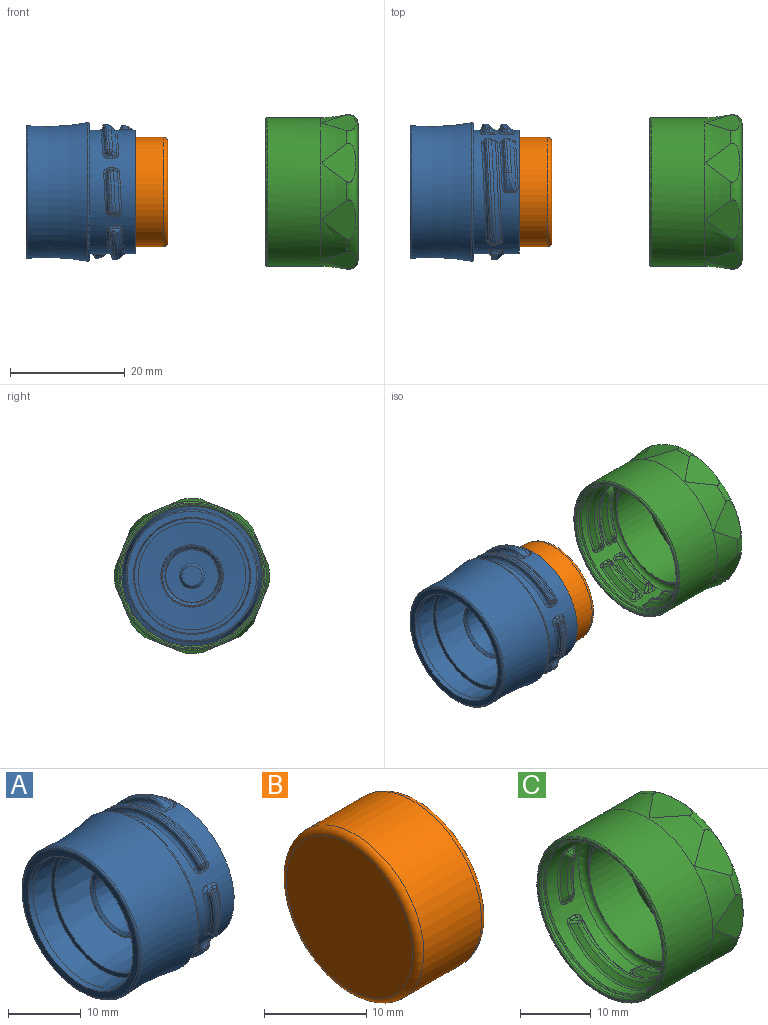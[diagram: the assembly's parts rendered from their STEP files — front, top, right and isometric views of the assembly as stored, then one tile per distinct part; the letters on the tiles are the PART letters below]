
ASSEMBLY  parts=3 mates=2
PART A: 206 faces, bbox 54.1x48.6x48.6 mm
  f0: bspline ~20.51x6.46mm, area 20.2mm2, adj f18,f76,f136,f188
  f1: bspline ~10.25x6.46mm, area 8.1mm2, adj f19,f60,f100,f196
  f2: bspline ~20.51x6.46mm, area 20.2mm2, adj f20,f106,f112,f156
  f3: bspline ~11.84x4.34mm, area 7mm2, adj f21,f82,f118,f180
  f4: bspline ~11.84x4.34mm, area 7mm2, adj f22,f88,f124,f172
  f5: bspline ~11.84x4.34mm, area 7mm2, adj f23,f94,f130,f164
  f6: bspline ~20.51x6.46mm, area 9.1mm2, adj f24,f81,f141,f195
  f7: bspline ~10.25x6.46mm, area 3.6mm2, adj f25,f63,f105,f203
  f8: bspline ~20.51x6.46mm, area 9.1mm2, adj f26,f111,f117,f163
  f9: bspline ~11.84x4.34mm, area 3.1mm2, adj f27,f87,f123,f187
  f10: bspline ~11.84x4.34mm, area 3.1mm2, adj f28,f93,f129,f179
  f11: bspline ~11.84x4.34mm, area 3.1mm2, adj f29,f99,f135,f171
  f12: cylinder r=11.84mm len=18.47mm, axis (-1,0,0), area 7.6mm2, adj f18,f24,f78,f80,f138,f139
  f13: cylinder r=11.84mm len=5.9mm, axis (-1,0,0), area 2.6mm2, adj f19,f25,f57,f102,f104
  f14: cylinder r=11.84mm len=18.47mm, axis (-1,0,0), area 7.6mm2, adj f20,f26,f108,f110,f114,f115
  f15: cylinder r=11.84mm len=7.03mm, axis (-1,0,0), area 2.6mm2, adj f21,f27,f84,f85,f120,f122
  f16: cylinder r=11.84mm len=7.03mm, axis (-1,0,0), area 2.6mm2, adj f22,f28,f90,f91,f126,f128
  f17: cylinder r=11.84mm len=7.03mm, axis (-1,0,0), area 2.6mm2, adj f23,f29,f96,f97,f132,f134
  f18: bspline ~19.36x5.44mm, area 12.6mm2, adj f0,f12,f77,f137
  f19: bspline ~7.42x4.83mm, area 4.3mm2, adj f1,f13,f60,f101
  f20: bspline ~19.93x5.61mm, area 12.6mm2, adj f2,f14,f107,f113
  f21: bspline ~8.49x1.01mm, area 4.3mm2, adj f3,f15,f83,f119
  f22: bspline ~8.49x1.09mm, area 4.3mm2, adj f4,f16,f89,f125
  f23: bspline ~8.48x1.05mm, area 4.3mm2, adj f5,f17,f95,f131
  f24: bspline ~19.36x5.35mm, area 7.4mm2, adj f6,f12,f80,f139
  f25: bspline ~7.72x4.94mm, area 2.5mm2, adj f7,f13,f63,f104
  f26: bspline ~19.35x5.52mm, area 7.4mm2, adj f8,f14,f110,f115
  f27: bspline ~8.48x1.03mm, area 2.5mm2, adj f9,f15,f85,f122
  f28: bspline ~8.48x1.11mm, area 2.5mm2, adj f10,f16,f91,f128
  f29: bspline ~8.48x1.01mm, area 2.5mm2, adj f11,f17,f97,f134
  f30: torus R=49.49mm, axis (1,0,0), area 766.5mm2, adj f204,f205
  f31: cone r=4.57mm half-angle=1deg, axis (-1,0,0), area 137.6mm2, adj f40,f46
  f32: cone r=9.55mm half-angle=88.5deg, axis (-1,0,0), area 193.8mm2, adj f36,f37
  f33: plane 22.56x22.56mm, normal (-1,0,0), area 74.4mm2, adj f47,f205
  f34: plane 20.17x20.17mm, normal (-1,0,0), area 43.5mm2, adj f35,f36
  f35: cone r=10.01mm half-angle=1deg, axis (1,0,0), area 224.6mm2, adj f34,f47
  f36: cone r=9.3mm half-angle=1deg, axis (1,0,0), area 617.8mm2, adj f32,f34
  f37: cone r=5.46mm half-angle=1deg, axis (1,0,0), area 261mm2, adj f32,f38
  f38: plane 10.61x10.61mm, normal (-1,0,0), area 5.7mm2, adj f37,f46
  f39: cone r=4.85mm half-angle=58.5deg, axis (-1,0,0), area 7.9mm2, adj f41,f45
  f40: cone r=4.22mm half-angle=58.5deg, axis (1,0,0), area 7.5mm2, adj f31,f41
  f41: cylinder r=4.85mm len=9.7mm, axis (1,0,0), area 11.6mm2, adj f39,f40
  f42: plane 3.51x3.51mm, normal (-1,0,0), area 9.6mm2, adj f43
  f43: cone r=1.75mm half-angle=45deg, axis (1,0,0), area 7.8mm2, adj f42,f44
  f44: cone r=9.55mm half-angle=88.5deg, axis (-1,0,0), area 51mm2, adj f43,f45
  f45: cone r=4.57mm half-angle=1deg, axis (-1,0,0), area 58.2mm2, adj f39,f44
  f46: cone r=5.13mm half-angle=45.5deg, axis (-1,0,0), area 17.9mm2, adj f31,f38
  f47: cone r=10.02mm half-angle=11deg, axis (-1,0,0), area 50.9mm2, adj f33,f35
  f48: plane 23.63x23.63mm, normal (1,0,0), area 74.3mm2, adj f49,f204
  f49: cylinder r=10.77mm len=21.54mm, axis (1,0,0), area 290.6mm2, adj f48,f52,f148,f149,f150,f151,f152,f153
  f50: plane 20.09x20.09mm, normal (1,0,0), area 317mm2, adj f51
  f51: cylinder r=10.04mm len=20.09mm, axis (1,0,0), area 195.6mm2, adj f50,f52
  f52: plane 21.54x21.54mm, normal (1,0,0), area 47.4mm2, adj f49,f51
  f53: bspline ~10.25x6.46mm, area 8.1mm2, adj f58,f59,f142,f148
  f54: bspline ~10.25x6.46mm, area 3.6mm2, adj f61,f62,f147,f155
  f55: cylinder r=11.84mm len=5.9mm, axis (-1,0,0), area 2.6mm2, adj f56,f59,f62,f144,f145
  f56: cylinder r=3.81mm len=3.21mm, axis (-1,0,0), area 2.4mm2, adj f55,f58,f61,f152
  f57: cylinder r=3.81mm len=3.21mm, axis (-1,0,0), area 2.4mm2, adj f13,f60,f63,f199
  f58: bspline ~4x1.34mm, area 2mm2, adj f53,f56,f59,f150
  f59: bspline ~6.61x4.58mm, area 4.3mm2, adj f53,f55,f58,f143
  f60: bspline ~4.04x1.6mm, area 2mm2, adj f1,f19,f57,f197
  f61: bspline ~3.63x0.96mm, area 1.1mm2, adj f54,f56,f62,f154
  f62: bspline ~7.86x4.78mm, area 2.5mm2, adj f54,f55,f61,f145
  f63: bspline ~4.19x0.96mm, area 1mm2, adj f7,f25,f57,f201
  f64: plane 0.75x0.38mm, normal (0,0.84,0.54), area 0.2mm2, adj f142,f143,f144,f147,f151
  f65: plane 0.75x0.45mm, normal (0,0.02,-1), area 0.2mm2, adj f130,f131,f132,f135,f168
  f66: plane 0.75x0.45mm, normal (0,0.02,-1), area 0.2mm2, adj f124,f125,f126,f129,f176
  f67: plane 0.75x0.38mm, normal (0,0.84,0.54), area 0.2mm2, adj f136,f137,f138,f141,f191
  f68: plane 0.75x0.38mm, normal (0,-0.84,-0.54), area 0.2mm2, adj f112,f113,f114,f117,f159
  f69: plane 0.75x0.45mm, normal (0,-0.02,1), area 0.2mm2, adj f118,f119,f120,f123,f184
  f70: plane 0.75x0.45mm, normal (0,0.02,1), area 0.2mm2, adj f94,f95,f96,f99,f167
  f71: plane 0.75x0.38mm, normal (0,0.84,-0.54), area 0.2mm2, adj f106,f107,f108,f111,f160
  f72: plane 0.75x0.45mm, normal (0,0.02,1), area 0.2mm2, adj f88,f89,f90,f93,f175
  f73: plane 0.75x0.38mm, normal (0,0.84,-0.54), area 0.2mm2, adj f100,f101,f102,f105,f200
  f74: plane 0.75x0.38mm, normal (0,-0.84,0.54), area 0.2mm2, adj f76,f77,f78,f81,f192
  f75: plane 0.75x0.45mm, normal (0,-0.02,-1), area 0.2mm2, adj f82,f83,f84,f87,f183
  f76: bspline ~1.4x1.37mm, area 0.5mm2, adj f0,f74,f77,f190
  f77: bspline ~0.71x0.7mm, area 0.3mm2, adj f18,f74,f76,f78
  f78: cylinder r=0.51mm len=0.59mm, axis (-1,0,0), area 0.2mm2, adj f12,f74,f77,f79
  f79: bspline ~0.66x0.46mm, area 0.1mm2, adj f78,f80,f81
  f80: bspline ~0.35x0.34mm, area 0mm2, adj f12,f24,f79,f81
  f81: bspline ~1.22x0.98mm, area 0.4mm2, adj f6,f74,f79,f80,f194
  f82: bspline ~1.35x1.33mm, area 0.5mm2, adj f3,f75,f83,f181
  f83: bspline ~0.74x0.57mm, area 0.3mm2, adj f21,f75,f82,f84
  f84: cylinder r=0.51mm len=0.48mm, axis (-1,0,0), area 0.2mm2, adj f15,f75,f83,f86
  f85: bspline ~0.32x0.27mm, area 0mm2, adj f15,f27,f86,f87
  f86: bspline ~0.5x0.46mm, area 0.1mm2, adj f84,f85,f87
  f87: bspline ~1.01x0.64mm, area 0.4mm2, adj f9,f75,f85,f86,f185
  f88: bspline ~1.35x1.33mm, area 0.5mm2, adj f4,f72,f89,f173
  f89: bspline ~0.74x0.57mm, area 0.3mm2, adj f22,f72,f88,f90
  f90: cylinder r=0.51mm len=0.48mm, axis (-1,0,0), area 0.2mm2, adj f16,f72,f89,f92
  f91: bspline ~0.32x0.27mm, area 0mm2, adj f16,f28,f92,f93
  f92: bspline ~0.5x0.46mm, area 0.1mm2, adj f90,f91,f93
  f93: bspline ~1.01x0.64mm, area 0.4mm2, adj f10,f72,f91,f92,f177
  f94: bspline ~1.35x1.33mm, area 0.5mm2, adj f5,f70,f95,f165
  f95: bspline ~0.74x0.57mm, area 0.3mm2, adj f23,f70,f94,f96
  f96: cylinder r=0.51mm len=0.48mm, axis (-1,0,0), area 0.2mm2, adj f17,f70,f95,f98
  f97: bspline ~0.32x0.27mm, area 0mm2, adj f17,f29,f98,f99
  f98: bspline ~0.5x0.46mm, area 0.1mm2, adj f96,f97,f99
  f99: bspline ~1.01x0.64mm, area 0.4mm2, adj f11,f70,f97,f98,f169
  f100: bspline ~1.4x1.37mm, area 0.5mm2, adj f1,f73,f101,f198
  f101: bspline ~0.71x0.7mm, area 0.3mm2, adj f19,f73,f100,f102
  f102: cylinder r=0.51mm len=0.59mm, axis (-1,0,0), area 0.2mm2, adj f13,f73,f101,f103
  f103: bspline ~0.66x0.46mm, area 0.1mm2, adj f102,f104,f105
  f104: bspline ~0.35x0.34mm, area 0mm2, adj f13,f25,f103,f105
  f105: bspline ~1.22x0.98mm, area 0.4mm2, adj f7,f73,f103,f104,f202
  f106: bspline ~1.4x1.37mm, area 0.5mm2, adj f2,f71,f107,f158
  f107: bspline ~0.71x0.7mm, area 0.3mm2, adj f20,f71,f106,f108
  f108: cylinder r=0.51mm len=0.59mm, axis (-1,0,0), area 0.2mm2, adj f14,f71,f107,f109
  f109: bspline ~0.66x0.46mm, area 0.1mm2, adj f108,f110,f111
  f110: bspline ~0.35x0.34mm, area 0mm2, adj f14,f26,f109,f111
  f111: bspline ~1.22x0.98mm, area 0.4mm2, adj f8,f71,f109,f110,f162
  f112: bspline ~1.41x1.38mm, area 0.5mm2, adj f2,f68,f113,f157
  f113: bspline ~0.74x0.67mm, area 0.3mm2, adj f20,f68,f112,f114
  f114: cylinder r=0.51mm len=0.59mm, axis (-1,0,0), area 0.2mm2, adj f14,f68,f113,f116
  f115: bspline ~0.35x0.34mm, area 0mm2, adj f14,f26,f116,f117
  f116: bspline ~0.66x0.46mm, area 0.1mm2, adj f114,f115,f117
  f117: bspline ~1.06x0.86mm, area 0.4mm2, adj f8,f68,f115,f116,f161
  f118: bspline ~1.36x1.32mm, area 0.5mm2, adj f3,f69,f119,f182
  f119: bspline ~0.7x0.61mm, area 0.3mm2, adj f21,f69,f118,f120
  f120: cylinder r=0.51mm len=0.48mm, axis (-1,0,0), area 0.2mm2, adj f15,f69,f119,f121
  f121: bspline ~0.5x0.46mm, area 0.1mm2, adj f120,f122,f123
  f122: bspline ~0.33x0.26mm, area 0mm2, adj f15,f27,f121,f123
  f123: bspline ~1.17x0.7mm, area 0.4mm2, adj f9,f69,f121,f122,f186
  f124: bspline ~1.36x1.32mm, area 0.5mm2, adj f4,f66,f125,f174
  f125: bspline ~0.7x0.61mm, area 0.3mm2, adj f22,f66,f124,f126
  f126: cylinder r=0.51mm len=0.48mm, axis (-1,0,0), area 0.2mm2, adj f16,f66,f125,f127
  f127: bspline ~0.5x0.46mm, area 0.1mm2, adj f126,f128,f129
  f128: bspline ~0.33x0.26mm, area 0mm2, adj f16,f28,f127,f129
  f129: bspline ~1.17x0.7mm, area 0.4mm2, adj f10,f66,f127,f128,f178
  f130: bspline ~1.36x1.32mm, area 0.5mm2, adj f5,f65,f131,f166
  f131: bspline ~0.7x0.61mm, area 0.3mm2, adj f23,f65,f130,f132
  f132: cylinder r=0.51mm len=0.48mm, axis (-1,0,0), area 0.2mm2, adj f17,f65,f131,f133
  f133: bspline ~0.5x0.46mm, area 0.1mm2, adj f132,f134,f135
  f134: bspline ~0.33x0.26mm, area 0mm2, adj f17,f29,f133,f135
  f135: bspline ~1.17x0.7mm, area 0.4mm2, adj f11,f65,f133,f134,f170
  f136: bspline ~1.41x1.38mm, area 0.5mm2, adj f0,f67,f137,f189
  f137: bspline ~0.74x0.67mm, area 0.3mm2, adj f18,f67,f136,f138
  f138: cylinder r=0.51mm len=0.59mm, axis (-1,0,0), area 0.2mm2, adj f12,f67,f137,f140
  f139: bspline ~0.35x0.34mm, area 0mm2, adj f12,f24,f140,f141
  f140: bspline ~0.66x0.46mm, area 0.1mm2, adj f138,f139,f141
  f141: bspline ~1.06x0.86mm, area 0.4mm2, adj f6,f67,f139,f140,f193
  f142: bspline ~1.41x1.38mm, area 0.5mm2, adj f53,f64,f143,f149
  f143: bspline ~0.74x0.67mm, area 0.3mm2, adj f59,f64,f142,f144
  f144: cylinder r=0.51mm len=0.59mm, axis (-1,0,0), area 0.2mm2, adj f55,f64,f143,f146
  f145: bspline ~0.35x0.34mm, area 0mm2, adj f55,f62,f146,f147
  f146: bspline ~0.66x0.46mm, area 0.1mm2, adj f144,f145,f147
  f147: bspline ~1.06x0.86mm, area 0.4mm2, adj f54,f64,f145,f146,f153
  f148: bspline ~10.19x6.22mm, area 3.7mm2, adj f49,f53,f149,f150
  f149: bspline ~1.52x0.78mm, area 0.5mm2, adj f49,f142,f148,f151
  f150: bspline ~1.23x0.84mm, area 0.3mm2, adj f49,f58,f148,f152
  f151: cylinder r=0.51mm len=0.75mm, axis (1,0,0), area 0.4mm2, adj f49,f64,f149,f153
  f152: cylinder r=0.51mm len=1.38mm, axis (1,0,0), area 0.4mm2, adj f49,f56,f150,f154
  f153: bspline ~1.17x1.03mm, area 0.7mm2, adj f49,f147,f151,f155
  f154: bspline ~1.45x0.75mm, area 0.7mm2, adj f49,f61,f152,f155
  f155: bspline ~10.24x5.89mm, area 6.2mm2, adj f49,f54,f153,f154
  f156: bspline ~19.7x6.27mm, area 8mm2, adj f2,f49,f157,f158
  f157: bspline ~1.52x0.78mm, area 0.5mm2, adj f49,f112,f156,f159
  f158: bspline ~1.5x0.83mm, area 0.5mm2, adj f49,f106,f156,f160
  f159: cylinder r=0.51mm len=0.75mm, axis (1,0,0), area 0.4mm2, adj f49,f68,f157,f161
  f160: cylinder r=0.51mm len=0.75mm, axis (1,0,0), area 0.4mm2, adj f49,f71,f158,f162
  f161: bspline ~1.17x1.03mm, area 0.7mm2, adj f49,f117,f159,f163
  f162: bspline ~1.21x1.2mm, area 0.7mm2, adj f49,f111,f160,f163
  f163: bspline ~19.45x5.88mm, area 14mm2, adj f8,f49,f161,f162
  f164: bspline ~10.04x1.63mm, area 2.8mm2, adj f5,f49,f165,f166
  f165: bspline ~1.52x0.83mm, area 0.5mm2, adj f49,f94,f164,f167
  f166: bspline ~1.5x0.91mm, area 0.5mm2, adj f49,f130,f164,f168
  f167: cylinder r=0.51mm len=0.75mm, axis (1,0,0), area 0.4mm2, adj f49,f70,f165,f169
  f168: cylinder r=0.51mm len=0.75mm, axis (1,0,0), area 0.4mm2, adj f49,f65,f166,f170
  f169: bspline ~1.11x1.03mm, area 0.7mm2, adj f49,f99,f167,f171
  f170: bspline ~1.2x1.19mm, area 0.7mm2, adj f49,f135,f168,f171
  f171: bspline ~8.76x1.55mm, area 4.8mm2, adj f11,f49,f169,f170
  f172: bspline ~10.04x1.63mm, area 2.8mm2, adj f4,f49,f173,f174
  f173: bspline ~1.52x0.83mm, area 0.5mm2, adj f49,f88,f172,f175
  f174: bspline ~1.5x0.91mm, area 0.5mm2, adj f49,f124,f172,f176
  f175: cylinder r=0.51mm len=0.75mm, axis (1,0,0), area 0.4mm2, adj f49,f72,f173,f177
  f176: cylinder r=0.51mm len=0.75mm, axis (1,0,0), area 0.4mm2, adj f49,f66,f174,f178
  f177: bspline ~1.11x1.03mm, area 0.7mm2, adj f49,f93,f175,f179
  f178: bspline ~1.2x1.19mm, area 0.7mm2, adj f49,f129,f176,f179
  f179: bspline ~9.91x1.55mm, area 4.8mm2, adj f10,f49,f177,f178
  f180: bspline ~10.04x1.63mm, area 2.8mm2, adj f3,f49,f181,f182
  f181: bspline ~1.52x0.83mm, area 0.5mm2, adj f49,f82,f180,f183
  f182: bspline ~1.5x0.91mm, area 0.5mm2, adj f49,f118,f180,f184
  f183: cylinder r=0.51mm len=0.75mm, axis (1,0,0), area 0.4mm2, adj f49,f75,f181,f185
  f184: cylinder r=0.51mm len=0.75mm, axis (1,0,0), area 0.4mm2, adj f49,f69,f182,f186
  f185: bspline ~1.11x1.03mm, area 0.7mm2, adj f49,f87,f183,f187
  f186: bspline ~1.2x1.19mm, area 0.7mm2, adj f49,f123,f184,f187
  f187: bspline ~8.76x1.55mm, area 4.8mm2, adj f9,f49,f185,f186
  f188: bspline ~19.7x6.27mm, area 8mm2, adj f0,f49,f189,f190
  f189: bspline ~1.52x0.78mm, area 0.5mm2, adj f49,f136,f188,f191
  f190: bspline ~1.5x0.83mm, area 0.5mm2, adj f49,f76,f188,f192
  f191: cylinder r=0.51mm len=0.75mm, axis (1,0,0), area 0.4mm2, adj f49,f67,f189,f193
  f192: cylinder r=0.51mm len=0.75mm, axis (1,0,0), area 0.4mm2, adj f49,f74,f190,f194
  f193: bspline ~1.17x1.03mm, area 0.7mm2, adj f49,f141,f191,f195
  f194: bspline ~1.21x1.2mm, area 0.7mm2, adj f49,f81,f192,f195
  f195: bspline ~19.45x5.88mm, area 14mm2, adj f6,f49,f193,f194
  f196: bspline ~10.13x6.26mm, area 3.7mm2, adj f1,f49,f197,f198
  f197: bspline ~1.32x1.04mm, area 0.4mm2, adj f49,f60,f196,f199
  f198: bspline ~1.17x0.83mm, area 0.5mm2, adj f49,f100,f196,f200
  f199: cylinder r=0.51mm len=1.35mm, axis (1,0,0), area 0.4mm2, adj f49,f57,f197,f201
  f200: cylinder r=0.51mm len=0.75mm, axis (1,0,0), area 0.4mm2, adj f49,f73,f198,f202
  f201: bspline ~1.79x0.73mm, area 0.6mm2, adj f49,f63,f199,f203
  f202: bspline ~1.21x1.2mm, area 0.7mm2, adj f49,f105,f200,f203
  f203: bspline ~10.24x5.83mm, area 6.2mm2, adj f7,f49,f201,f202
  f204: torus R=11.82mm, axis (-1,0,0), area 33.7mm2, adj f30,f48
  f205: torus R=11.28mm, axis (-1,0,0), area 30.3mm2, adj f30,f33
PART B: 5 faces, bbox 9.5x20.6x20.6 mm
  f0: cylinder r=9.53mm len=19.05mm, axis (-1,0,0), area 478.8mm2, adj f3,f4
  f1: plane 17.53x17.53mm, normal (1,0,0), area 241.2mm2, adj f4
  f2: plane 17.53x17.53mm, normal (-1,0,0), area 241.2mm2, adj f3
  f3: torus R=8.76mm, axis (1,0,0), area 69.6mm2, adj f0,f2
  f4: torus R=8.76mm, axis (1,0,0), area 69.6mm2, adj f0,f1
PART C: 209 faces, bbox 31.3x42x42 mm
  f0: plane 5.84x5.24mm, normal (0,-0.71,0.71), area 25.5mm2, adj f202,f207
  f1: plane 7.67x6.09mm, normal (0,0,1), area 25.5mm2, adj f202,f207
  f2: plane 5.84x5.24mm, normal (0,0.71,0.71), area 25.5mm2, adj f202,f207
  f3: plane 7.42x5.84mm, normal (0,1,0), area 25.5mm2, adj f202,f207
  f4: plane 5.84x5.24mm, normal (0,0.71,-0.71), area 25.5mm2, adj f202,f207
  f5: plane 7.65x6.07mm, normal (0,0,-1), area 25.5mm2, adj f202,f207
  f6: plane 5.84x5.24mm, normal (0,-0.71,-0.71), area 25.5mm2, adj f202,f207
  f7: bspline ~11.96x4.38mm, area 7.2mm2, adj f25,f99,f105,f167
  f8: bspline ~20.72x6.52mm, area 20.5mm2, adj f26,f111,f117,f159
  f9: bspline ~11.96x4.38mm, area 7.2mm2, adj f27,f75,f87,f183
  f10: bspline ~11.96x4.38mm, area 7.2mm2, adj f28,f123,f135,f151
  f11: bspline ~20.72x6.52mm, area 20.5mm2, adj f29,f81,f93,f175
  f12: bspline ~10.36x6.52mm, area 8.9mm2, adj f30,f51,f129,f143
  f13: cylinder r=10.9mm len=16.83mm, axis (1,0,0), area 6.9mm2, adj f29,f35,f83,f85,f95,f96
  f14: cylinder r=10.9mm len=6.21mm, axis (1,0,0), area 2.3mm2, adj f25,f31,f101,f103,f107,f108
  f15: cylinder r=10.9mm len=16.83mm, axis (1,0,0), area 6.9mm2, adj f26,f32,f113,f115,f119,f120
  f16: cylinder r=10.9mm len=6.26mm, axis (1,0,0), area 2.7mm2, adj f50,f52,f55,f71,f72
  f17: cylinder r=10.9mm len=6.21mm, axis (1,0,0), area 2.3mm2, adj f28,f34,f125,f127,f137,f138
  f18: cylinder r=10.9mm len=6.21mm, axis (1,0,0), area 2.3mm2, adj f27,f33,f77,f79,f89,f90
  f19: bspline ~11.96x4.38mm, area 2.9mm2, adj f31,f104,f110,f174
  f20: bspline ~20.72x6.52mm, area 8.9mm2, adj f32,f116,f122,f166
  f21: bspline ~11.96x4.38mm, area 2.9mm2, adj f33,f80,f92,f190
  f22: bspline ~11.96x4.38mm, area 2.9mm2, adj f34,f128,f140,f158
  f23: bspline ~20.72x6.52mm, area 8.9mm2, adj f35,f86,f98,f182
  f24: bspline ~10.36x6.52mm, area 3.8mm2, adj f36,f54,f134,f150
  f25: bspline ~7.95x1.09mm, area 3.8mm2, adj f7,f14,f100,f106
  f26: bspline ~18.19x4.86mm, area 11.6mm2, adj f8,f15,f112,f118
  f27: bspline ~7.96x1.01mm, area 3.8mm2, adj f9,f18,f76,f88
  f28: bspline ~7.96x1.08mm, area 3.8mm2, adj f10,f17,f124,f136
  f29: bspline ~18.18x4.99mm, area 11.6mm2, adj f11,f13,f82,f94
  f30: bspline ~9.21x5.04mm, area 4.5mm2, adj f12,f47,f51,f130
  f31: bspline ~7.07x0.86mm, area 2.1mm2, adj f14,f19,f103,f108
  f32: bspline ~17.61x4.55mm, area 6.8mm2, adj f15,f20,f115,f120
  f33: bspline ~7.07x0.8mm, area 2.1mm2, adj f18,f21,f79,f90
  f34: bspline ~7.95x0.93mm, area 2.1mm2, adj f17,f22,f127,f138
  f35: bspline ~18.16x4.96mm, area 6.8mm2, adj f13,f23,f85,f96
  f36: bspline ~8.33x4.52mm, area 2.6mm2, adj f24,f47,f54,f133
  f37: plane 21.95x21.95mm, normal (-1,0,0), area 59.8mm2, adj f39,f201
  f38: cylinder r=11.96mm len=23.93mm, axis (1,0,0), area 223.5mm2, adj f142,f143,f144,f145,f146,f147,f148,f151
  f39: cone r=9.98mm half-angle=5deg, axis (1,0,0), area 62.6mm2, adj f37,f40
  f40: plane 19.96x19.96mm, normal (-1,0,0), area 12.6mm2, adj f39,f42
  f41: plane 19.56x19.56mm, normal (-1,0,0), area 300.4mm2, adj f42
  f42: cylinder r=9.78mm len=19.56mm, axis (1,0,0), area 460.4mm2, adj f40,f41
  f43: cylinder r=12.22mm len=24.43mm, axis (-1,0,0), area 39mm2, adj f141,f142
  f44: cylinder r=12.95mm len=25.91mm, axis (1,0,0), area 754.6mm2, adj f202,f208
  f45: plane 25.4x25.4mm, normal (-1,0,0), area 18.1mm2, adj f141,f208
  f46: bspline ~10.36x6.52mm, area 8.8mm2, adj f52,f53,f69,f191,f193
  f47: cylinder r=10.9mm len=6.26mm, axis (1,0,0), area 2.7mm2, adj f30,f36,f49,f131,f133
  f48: bspline ~10.36x6.52mm, area 3.8mm2, adj f55,f56,f74,f200
  f49: cylinder r=3.81mm len=2.02mm, axis (1,0,0), area 1.8mm2, adj f47,f51,f54,f147
  f50: cylinder r=3.81mm len=2.02mm, axis (1,0,0), area 1.8mm2, adj f16,f53,f56,f196
  f51: bspline ~2.72x1.34mm, area 1.5mm2, adj f12,f30,f49,f145
  f52: bspline ~7.8x5.05mm, area 4.5mm2, adj f16,f46,f53,f70
  f53: bspline ~2.91x1.63mm, area 1.6mm2, adj f46,f50,f52,f192,f194
  f54: bspline ~3.09x1.58mm, area 0.8mm2, adj f24,f36,f49,f149
  f55: bspline ~7.47x4.74mm, area 2.6mm2, adj f16,f48,f56,f72
  f56: bspline ~3.08x1.57mm, area 0.7mm2, adj f48,f50,f55,f198
  f57: plane 1.01x0.83mm, normal (0,0.02,1), area 0.5mm2, adj f129,f130,f131,f134,f146
  f58: plane 1.01x0.7mm, normal (0,0.84,-0.54), area 0.5mm2, adj f135,f136,f137,f140,f155
  f59: plane 1.01x0.83mm, normal (0,0.02,1), area 0.5mm2, adj f81,f82,f83,f86,f178
  f60: plane 1.01x0.7mm, normal (0,0.84,-0.54), area 0.5mm2, adj f87,f88,f89,f92,f187
  f61: plane 1.01x0.7mm, normal (0,0.84,0.54), area 0.5mm2, adj f123,f124,f125,f128,f154
  f62: plane 1.01x0.83mm, normal (0,0.02,-1), area 0.5mm2, adj f117,f118,f119,f122,f163
  f63: plane 1.01x0.83mm, normal (0,0.02,-1), area 0.5mm2, adj f69,f70,f71,f74,f197
  f64: plane 1.01x0.7mm, normal (0,0.84,0.54), area 0.5mm2, adj f75,f76,f77,f80,f186
  f65: plane 1.01x0.7mm, normal (0,-0.84,0.54), area 0.5mm2, adj f105,f106,f107,f110,f171
  f66: plane 1.01x0.83mm, normal (0,-0.02,-1), area 0.5mm2, adj f111,f112,f113,f116,f162
  f67: plane 1.01x0.83mm, normal (0,-0.02,1), area 0.5mm2, adj f93,f94,f95,f98,f179
  f68: plane 1.01x0.7mm, normal (0,-0.84,-0.54), area 0.5mm2, adj f99,f100,f101,f104,f170
  f69: bspline ~1.82x1.54mm, area 0.6mm2, adj f46,f63,f70,f195
  f70: bspline ~0.71x0.5mm, area 0.2mm2, adj f52,f63,f69,f71
  f71: cylinder r=0.51mm len=0.38mm, axis (1,0,0), area 0.1mm2, adj f16,f63,f70,f73
  f72: bspline ~0.49x0.39mm, area 0.1mm2, adj f16,f55,f73,f74
  f73: bspline ~0.44x0.41mm, area 0mm2, adj f71,f72,f74
  f74: bspline ~1.52x0.74mm, area 0.6mm2, adj f48,f63,f72,f73,f199
  f75: bspline ~1.67x1.59mm, area 0.6mm2, adj f9,f64,f76,f184
  f76: bspline ~0.68x0.55mm, area 0.2mm2, adj f27,f64,f75,f77
  f77: cylinder r=0.51mm len=0.42mm, axis (1,0,0), area 0.1mm2, adj f18,f64,f76,f78
  f78: bspline ~0.51x0.42mm, area 0mm2, adj f77,f79,f80
  f79: bspline ~0.44x0.35mm, area 0.1mm2, adj f18,f33,f78,f80
  f80: bspline ~1.5x1.15mm, area 0.6mm2, adj f21,f64,f78,f79,f188
  f81: bspline ~1.8x1.59mm, area 0.6mm2, adj f11,f59,f82,f176
  f82: bspline ~0.68x0.54mm, area 0.2mm2, adj f29,f59,f81,f83
  f83: cylinder r=0.51mm len=0.38mm, axis (1,0,0), area 0.1mm2, adj f13,f59,f82,f84
  f84: bspline ~0.44x0.42mm, area 0mm2, adj f83,f85,f86
  f85: bspline ~0.48x0.38mm, area 0.1mm2, adj f13,f35,f84,f86
  f86: bspline ~1.5x0.66mm, area 0.6mm2, adj f23,f59,f84,f85,f180
  f87: bspline ~1.67x1.54mm, area 0.6mm2, adj f9,f60,f88,f185
  f88: bspline ~0.71x0.52mm, area 0.2mm2, adj f27,f60,f87,f89
  f89: cylinder r=0.51mm len=0.42mm, axis (1,0,0), area 0.1mm2, adj f18,f60,f88,f91
  f90: bspline ~0.51x0.38mm, area 0.1mm2, adj f18,f33,f91,f92
  f91: bspline ~0.51x0.41mm, area 0mm2, adj f89,f90,f92
  f92: bspline ~1.54x1.18mm, area 0.6mm2, adj f21,f60,f90,f91,f189
  f93: bspline ~1.82x1.54mm, area 0.6mm2, adj f11,f67,f94,f177
  f94: bspline ~0.71x0.5mm, area 0.2mm2, adj f29,f67,f93,f95
  f95: cylinder r=0.51mm len=0.38mm, axis (1,0,0), area 0.1mm2, adj f13,f67,f94,f97
  f96: bspline ~0.49x0.39mm, area 0.1mm2, adj f13,f35,f97,f98
  f97: bspline ~0.44x0.41mm, area 0mm2, adj f95,f96,f98
  f98: bspline ~1.52x0.74mm, area 0.6mm2, adj f23,f67,f96,f97,f181
  f99: bspline ~1.67x1.59mm, area 0.6mm2, adj f7,f68,f100,f168
  f100: bspline ~0.68x0.55mm, area 0.2mm2, adj f25,f68,f99,f101
  f101: cylinder r=0.51mm len=0.42mm, axis (1,0,0), area 0.1mm2, adj f14,f68,f100,f102
  f102: bspline ~0.51x0.42mm, area 0mm2, adj f101,f103,f104
  f103: bspline ~0.44x0.35mm, area 0.1mm2, adj f14,f31,f102,f104
  f104: bspline ~1.5x1.15mm, area 0.6mm2, adj f19,f68,f102,f103,f172
  f105: bspline ~1.67x1.54mm, area 0.6mm2, adj f7,f65,f106,f169
  f106: bspline ~0.71x0.52mm, area 0.2mm2, adj f25,f65,f105,f107
  f107: cylinder r=0.51mm len=0.42mm, axis (1,0,0), area 0.1mm2, adj f14,f65,f106,f109
  f108: bspline ~0.51x0.38mm, area 0.1mm2, adj f14,f31,f109,f110
  f109: bspline ~0.51x0.41mm, area 0mm2, adj f107,f108,f110
  f110: bspline ~1.54x1.18mm, area 0.6mm2, adj f19,f65,f108,f109,f173
  f111: bspline ~1.8x1.59mm, area 0.6mm2, adj f8,f66,f112,f160
  f112: bspline ~0.68x0.54mm, area 0.2mm2, adj f26,f66,f111,f113
  f113: cylinder r=0.51mm len=0.38mm, axis (1,0,0), area 0.1mm2, adj f15,f66,f112,f114
  f114: bspline ~0.44x0.42mm, area 0mm2, adj f113,f115,f116
  f115: bspline ~0.48x0.38mm, area 0.1mm2, adj f15,f32,f114,f116
  f116: bspline ~1.5x0.66mm, area 0.6mm2, adj f20,f66,f114,f115,f164
  f117: bspline ~1.82x1.54mm, area 0.6mm2, adj f8,f62,f118,f161
  f118: bspline ~0.71x0.5mm, area 0.2mm2, adj f26,f62,f117,f119
  f119: cylinder r=0.51mm len=0.38mm, axis (1,0,0), area 0.1mm2, adj f15,f62,f118,f121
  f120: bspline ~0.49x0.39mm, area 0.1mm2, adj f15,f32,f121,f122
  f121: bspline ~0.44x0.41mm, area 0mm2, adj f119,f120,f122
  f122: bspline ~1.52x0.74mm, area 0.6mm2, adj f20,f62,f120,f121,f165
  f123: bspline ~1.67x1.59mm, area 0.6mm2, adj f10,f61,f124,f152
  f124: bspline ~0.68x0.55mm, area 0.2mm2, adj f28,f61,f123,f125
  f125: cylinder r=0.51mm len=0.42mm, axis (1,0,0), area 0.1mm2, adj f17,f61,f124,f126
  f126: bspline ~0.51x0.42mm, area 0mm2, adj f125,f127,f128
  f127: bspline ~0.44x0.35mm, area 0.1mm2, adj f17,f34,f126,f128
  f128: bspline ~1.5x1.15mm, area 0.6mm2, adj f22,f61,f126,f127,f156
  f129: bspline ~1.8x1.59mm, area 0.6mm2, adj f12,f57,f130,f144
  f130: bspline ~0.68x0.54mm, area 0.2mm2, adj f30,f57,f129,f131
  f131: cylinder r=0.51mm len=0.38mm, axis (1,0,0), area 0.1mm2, adj f47,f57,f130,f132
  f132: bspline ~0.44x0.42mm, area 0mm2, adj f131,f133,f134
  f133: bspline ~0.48x0.38mm, area 0.1mm2, adj f36,f47,f132,f134
  f134: bspline ~1.5x0.66mm, area 0.6mm2, adj f24,f57,f132,f133,f148
  f135: bspline ~1.67x1.54mm, area 0.6mm2, adj f10,f58,f136,f153
  f136: bspline ~0.71x0.52mm, area 0.2mm2, adj f28,f58,f135,f137
  f137: cylinder r=0.51mm len=0.42mm, axis (1,0,0), area 0.1mm2, adj f17,f58,f136,f139
  f138: bspline ~0.51x0.38mm, area 0.1mm2, adj f17,f34,f139,f140
  f139: bspline ~0.51x0.41mm, area 0mm2, adj f137,f138,f140
  f140: bspline ~1.54x1.18mm, area 0.6mm2, adj f22,f58,f138,f139,f157
  f141: torus R=12.47mm, axis (-1,0,0), area 30.9mm2, adj f43,f45
  f142: torus R=12.22mm, axis (-1,0,0), area 30.2mm2, adj f38,f43,f191,f192
  f143: bspline ~12.58x6.96mm, area 4.2mm2, adj f12,f38,f144,f145
  f144: bspline ~1.19x0.87mm, area 0.4mm2, adj f38,f129,f143,f146
  f145: bspline ~1.24x0.98mm, area 0.4mm2, adj f38,f51,f143,f147
  f146: cylinder r=0.51mm len=1.01mm, axis (1,0,0), area 0.5mm2, adj f38,f57,f144,f148
  f147: cylinder r=0.51mm len=1.21mm, axis (-1,0,0), area 0.5mm2, adj f38,f49,f145,f149,f201
  f148: bspline ~1.15x1.06mm, area 0.6mm2, adj f38,f134,f146,f150,f201
  f149: bspline ~1.62x0.7mm, area 0.2mm2, adj f54,f147,f150,f201
  f150: bspline ~11.31x6.21mm, area 4mm2, adj f24,f148,f149,f201
  f151: bspline ~12.33x1.84mm, area 3.3mm2, adj f10,f38,f152,f153
  f152: bspline ~0.99x0.93mm, area 0.4mm2, adj f38,f123,f151,f154
  f153: bspline ~1.18x0.77mm, area 0.4mm2, adj f38,f135,f151,f155
  f154: cylinder r=0.51mm len=1.01mm, axis (1,0,0), area 0.5mm2, adj f38,f61,f152,f156
  f155: cylinder r=0.51mm len=1.01mm, axis (1,0,0), area 0.5mm2, adj f38,f58,f153,f157
  f156: bspline ~1.47x1.15mm, area 0.7mm2, adj f38,f128,f154,f158
  f157: bspline ~1.51x0.97mm, area 0.7mm2, adj f38,f140,f155,f158,f201
  f158: bspline ~9.28x1.59mm, area 4.7mm2, adj f22,f38,f156,f157,f201
  f159: bspline ~21.71x6.97mm, area 8.9mm2, adj f8,f38,f160,f161
  f160: bspline ~1.19x0.87mm, area 0.4mm2, adj f38,f111,f159,f162
  f161: bspline ~1.18x0.65mm, area 0.4mm2, adj f38,f117,f159,f163
  f162: cylinder r=0.51mm len=1.01mm, axis (1,0,0), area 0.5mm2, adj f38,f66,f160,f164
  f163: cylinder r=0.51mm len=1.01mm, axis (1,0,0), area 0.5mm2, adj f38,f62,f161,f165
  f164: bspline ~1.22x1.2mm, area 0.7mm2, adj f38,f116,f162,f166
  f165: bspline ~1.26x1.25mm, area 0.7mm2, adj f38,f122,f163,f166
  f166: bspline ~20.74x6.2mm, area 15.1mm2, adj f20,f38,f164,f165
  f167: bspline ~12.33x1.84mm, area 3.3mm2, adj f7,f38,f168,f169
  f168: bspline ~0.99x0.93mm, area 0.4mm2, adj f38,f99,f167,f170
  f169: bspline ~1.18x0.77mm, area 0.4mm2, adj f38,f105,f167,f171
  f170: cylinder r=0.51mm len=1.01mm, axis (1,0,0), area 0.5mm2, adj f38,f68,f168,f172
  f171: cylinder r=0.51mm len=1.01mm, axis (1,0,0), area 0.5mm2, adj f38,f65,f169,f173
  f172: bspline ~1.47x1.15mm, area 0.7mm2, adj f38,f104,f170,f174
  f173: bspline ~1.51x0.97mm, area 0.7mm2, adj f38,f110,f171,f174
  f174: bspline ~9.28x1.59mm, area 5.1mm2, adj f19,f38,f172,f173
  f175: bspline ~21.71x6.97mm, area 8.9mm2, adj f11,f38,f176,f177
  f176: bspline ~0.93x0.87mm, area 0.4mm2, adj f38,f81,f175,f178
  f177: bspline ~1.18x0.65mm, area 0.4mm2, adj f38,f93,f175,f179
  f178: cylinder r=0.51mm len=1.01mm, axis (1,0,0), area 0.5mm2, adj f38,f59,f176,f180
  f179: cylinder r=0.51mm len=1.01mm, axis (1,0,0), area 0.5mm2, adj f38,f67,f177,f181
  f180: bspline ~1.15x1.06mm, area 0.7mm2, adj f38,f86,f178,f182
  f181: bspline ~1.26x1.25mm, area 0.7mm2, adj f38,f98,f179,f182
  f182: bspline ~20.74x6.2mm, area 15.1mm2, adj f23,f38,f180,f181
  f183: bspline ~12.33x1.84mm, area 3.3mm2, adj f9,f38,f184,f185
  f184: bspline ~0.99x0.93mm, area 0.4mm2, adj f38,f75,f183,f186
  f185: bspline ~1.18x0.77mm, area 0.4mm2, adj f38,f87,f183,f187
  f186: cylinder r=0.51mm len=1.01mm, axis (1,0,0), area 0.5mm2, adj f38,f64,f184,f188
  f187: cylinder r=0.51mm len=1.01mm, axis (1,0,0), area 0.5mm2, adj f38,f60,f185,f189
  f188: bspline ~1.47x1.15mm, area 0.7mm2, adj f38,f80,f186,f190
  f189: bspline ~1.51x0.97mm, area 0.7mm2, adj f38,f92,f187,f190
  f190: bspline ~9.28x1.59mm, area 5.1mm2, adj f21,f38,f188,f189
  f191: bspline ~2.52x0.51mm, area 0.5mm2, adj f46,f142,f192,f193
  f192: bspline ~0.92x0.44mm, area 0.1mm2, adj f53,f142,f191,f194
  f193: bspline ~10.18x6.95mm, area 3.6mm2, adj f38,f46,f191,f195
  f194: bspline ~1.24x0.74mm, area 0.3mm2, adj f38,f53,f192,f196
  f195: bspline ~1.18x0.65mm, area 0.4mm2, adj f38,f69,f193,f197
  f196: cylinder r=0.51mm len=1.18mm, axis (-1,0,0), area 0.5mm2, adj f38,f50,f194,f198
  f197: cylinder r=0.51mm len=1.01mm, axis (1,0,0), area 0.5mm2, adj f38,f63,f195,f199
  f198: bspline ~1.56x0.85mm, area 0.5mm2, adj f38,f56,f196,f200
  f199: bspline ~1.26x1.25mm, area 0.7mm2, adj f38,f74,f197,f200
  f200: bspline ~10.44x6.16mm, area 7mm2, adj f38,f48,f198,f199
  f201: torus R=10.97mm, axis (-1,0,0), area 108mm2, adj f37,f38,f147,f148,f149,f150,f157,f158
  f202: torus R=34.79mm, axis (1,0,0), area 248.2mm2, adj f0,f1,f2,f3,f4,f5,f6,f44
  f203: plane 23.78x23.78mm, normal (1,0,0), area 143.6mm2, adj f205,f207
  f204: plane 7.42x5.84mm, normal (0,-1,0), area 25.5mm2, adj f202,f207
  f205: cylinder r=9.78mm len=19.56mm, axis (1,0,0), area 15.6mm2, adj f203,f206
  f206: plane 19.56x19.56mm, normal (1,0,0), area 300.4mm2, adj f205
  f207: torus R=11.89mm, axis (-1,0,0), area 148.9mm2, adj f0,f1,f2,f3,f4,f5,f6,f202
  f208: torus R=12.7mm, axis (-1,0,0), area 32.2mm2, adj f44,f45
PLACE A t=(0,1.59,2.67)mm fixed
PLACE B t=(-3.86,1.59,2.67)mm
PLACE C rot(axis=(1,0,0),111.9deg) t=(38.79,1.59,2.67)mm
MATE cylindrical C.f13 <-> A.f12  axis (1,0,0) through (27.04,1.59,2.67)mm
MATE fastened B.f0 <-> A.f12  axis (-1,0,0) through (-3.1,1.59,2.67)mm
